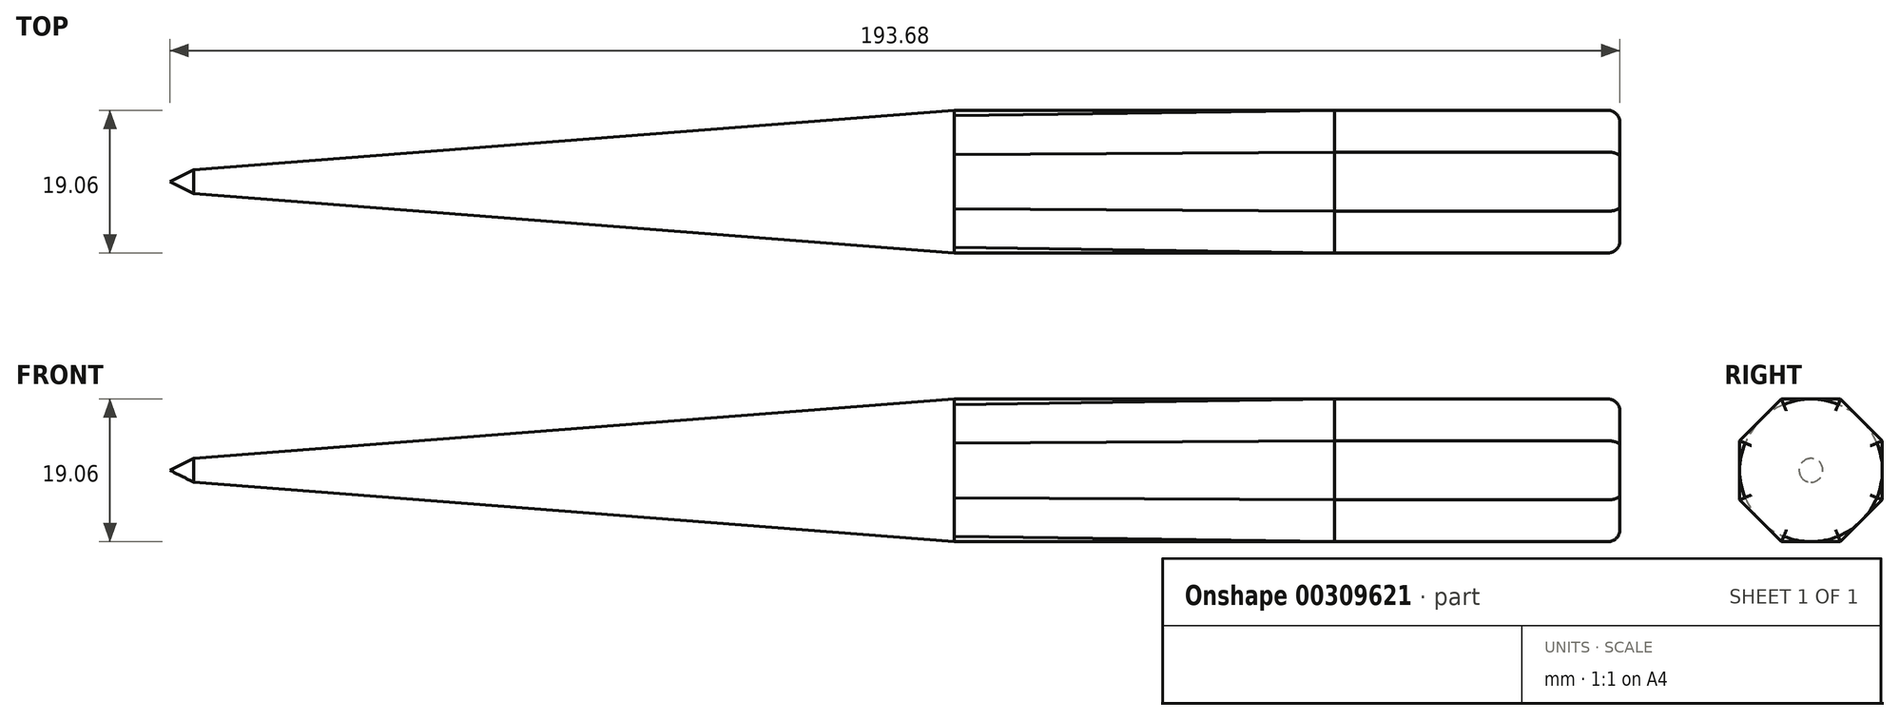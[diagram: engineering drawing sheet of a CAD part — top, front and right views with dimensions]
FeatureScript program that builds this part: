
annotation { "Feature Type Name" : "Feature", "Feature Type Description" : "" }
export const myFeature = defineFeature(function(context is Context, id is Id, definition is map)
    precondition{}
    {
        {
            var Q0;
            Q0=qCreatedBy(makeId("Right.planeOp"),FACE);
            var sketch = newSketch(context, id + "F0", { "sketchPlane" : qUnion([Q0])});
            skCircle(sketch, "E0.cCircle", {"center": v(0, 0) * mm, "radius": 9.53 * mm, "construction": true});
            skLineSegment(sketch, "E0.0", {"start": v(9.53, 3.95) * mm, "end": v(9.53, -3.95) * mm});
            skLineSegment(sketch, "E0.1", {"start": v(9.53, -3.95) * mm, "end": v(3.95, -9.53) * mm});
            skLineSegment(sketch, "E0.2", {"start": v(3.95, -9.53) * mm, "end": v(-3.95, -9.53) * mm});
            skLineSegment(sketch, "E0.3", {"start": v(-3.95, -9.53) * mm, "end": v(-9.53, -3.95) * mm});
            skLineSegment(sketch, "E0.4", {"start": v(-9.53, -3.95) * mm, "end": v(-9.53, 3.95) * mm});
            skLineSegment(sketch, "E0.5", {"start": v(-9.53, 3.95) * mm, "end": v(-3.95, 9.52) * mm});
            skLineSegment(sketch, "E0.6", {"start": v(-3.95, 9.52) * mm, "end": v(3.95, 9.53) * mm});
            skLineSegment(sketch, "E0.7", {"start": v(3.95, 9.53) * mm, "end": v(9.53, 3.95) * mm});
            skPoint(sketch, "E0.0.midPoint", {"position": v(9.53, 0) * mm});
            skSolve(sketch);
        }
        {
            var Q0;
            Q0=makeQuery(id+"F0.imprint","IMPRINT",FACE,{"disambiguationData":[TD([[makeQuery(id+"F0.imprint","IMPRINT",EDGE,{"derivedFrom":sQuery(id+"F0.wireOp",EDGE,"E0.0")}),-1.0]])]});
            extrude(context, id + "F1", {"entities" : qUnion([Q0]), "oppositeDirection" : true, "depth" : 38.1 * mm});
        }
        {
            var Q0;
            Q0=makeQuery(id+"F1.opExtrude","CAP_FACE",FACE,{"disambiguationData":[OSD([sQuery(id+"F0.wireOp",EDGE,"E0.0"),sQuery(id+"F0.wireOp",EDGE,"E0.1"),sQuery(id+"F0.wireOp",EDGE,"E0.2"),sQuery(id+"F0.wireOp",EDGE,"E0.3"),sQuery(id+"F0.wireOp",EDGE,"E0.4"),sQuery(id+"F0.wireOp",EDGE,"E0.5"),sQuery(id+"F0.wireOp",EDGE,"E0.6"),sQuery(id+"F0.wireOp",EDGE,"E0.7")])],"isStart":false});
            cPlane(context, id + "F2", {"entities" : qUnion([Q0]), "cplaneType" : CPlaneType.OFFSET, "offset" : 50.8 * mm, "width" : 152.4 * mm, "height" : 152.4 * mm});
        }
        {
            var Q0;
            Q0=qCreatedBy(id+"F2.planeOp",FACE);
            var sketch = newSketch(context, id + "F3", { "sketchPlane" : qUnion([Q0])});
            skCircle(sketch, "E1", {"center": v(0, 0) * mm, "radius": 9.53 * mm});
            skSolve(sketch);
        }
        {
            var Q1;
            Q1=makeQuery(id+"F1.opExtrude","CAP_FACE",FACE,{"disambiguationData":[OSD([sQuery(id+"F0.wireOp",EDGE,"E0.0"),sQuery(id+"F0.wireOp",EDGE,"E0.1"),sQuery(id+"F0.wireOp",EDGE,"E0.2"),sQuery(id+"F0.wireOp",EDGE,"E0.3"),sQuery(id+"F0.wireOp",EDGE,"E0.4"),sQuery(id+"F0.wireOp",EDGE,"E0.5"),sQuery(id+"F0.wireOp",EDGE,"E0.6"),sQuery(id+"F0.wireOp",EDGE,"E0.7")])],"isStart":false});
            var Q2;
            Q2=makeQuery(id+"F3.imprint","IMPRINT",FACE,{"disambiguationData":[TD([[makeQuery(id+"F3.imprint","IMPRINT",EDGE,{"derivedFrom":sQuery(id+"F3.wireOp",EDGE,"E1")}),1.0]])]});
            loft(context, id + "F4", {"operationType" : NewBodyOperationType.ADD, "sheetProfilesArray" : [{ "sheetProfileEntities" : qUnion([Q1]) }, { "sheetProfileEntities" : qUnion([Q2]) }]});
        }
        {
            var Q0;
            Q0=makeQuery(id+"F4.opLoft","CAP_FACE",FACE,{"disambiguationData":[OSD([makeQuery(id+"F3.imprint","IMPRINT",FACE,{"disambiguationData":[TD([[makeQuery(id+"F3.imprint","IMPRINT",EDGE,{"derivedFrom":sQuery(id+"F3.wireOp",EDGE,"E1")}),1.0]])]})])],"isStart":true});
            cPlane(context, id + "F5", {"entities" : qUnion([Q0]), "cplaneType" : CPlaneType.OFFSET, "offset" : 101.6 * mm, "width" : 152.4 * mm, "height" : 152.4 * mm});
        }
        {
            var Q0;
            Q0=qCreatedBy(id+"F5.planeOp",FACE);
            var sketch = newSketch(context, id + "F6", { "sketchPlane" : qUnion([Q0])});
            skCircle(sketch, "E2", {"center": v(0, 0) * mm, "radius": 1.59 * mm});
            skSolve(sketch);
        }
        {
            var Q1;
            Q1=makeQuery(id+"F4.opLoft","CAP_FACE",FACE,{"disambiguationData":[OSD([makeQuery(id+"F3.imprint","IMPRINT",FACE,{"disambiguationData":[TD([[makeQuery(id+"F3.imprint","IMPRINT",EDGE,{"derivedFrom":sQuery(id+"F3.wireOp",EDGE,"E1")}),1.0]])]})])],"isStart":true});
            var Q2;
            Q2=makeQuery(id+"F6.imprint","IMPRINT",FACE,{"disambiguationData":[TD([[makeQuery(id+"F6.imprint","IMPRINT",EDGE,{"derivedFrom":sQuery(id+"F6.wireOp",EDGE,"E2")}),1.0]])]});
            loft(context, id + "F7", {"operationType" : NewBodyOperationType.ADD, "sheetProfilesArray" : [{ "sheetProfileEntities" : qUnion([Q1]) }, { "sheetProfileEntities" : qUnion([Q2]) }]});
        }
        {
            var Q0;
            Q0=qCreatedBy(id+"F5.planeOp",FACE);
            cPlane(context, id + "F8", {"entities" : qUnion([Q0]), "cplaneType" : CPlaneType.OFFSET, "offset" : 3.17 * mm, "width" : 152.4 * mm, "height" : 152.4 * mm});
        }
        {
            var Q0;
            Q0=qCreatedBy(id+"F8.planeOp",FACE);
            var sketch = newSketch(context, id + "F9", { "sketchPlane" : qUnion([Q0])});
            skPoint(sketch, "E3", {"position": v(0, 0) * mm});
            skSolve(sketch);
        }
        {
            var Q1;
            Q1=sQuery(id+"F9.wireOp",VERTEX,"E3");
            var Q2;
            Q2=makeQuery(id+"F7.opLoft","CAP_FACE",FACE,{"disambiguationData":[OSD([makeQuery(id+"F6.imprint","IMPRINT",FACE,{"disambiguationData":[TD([[makeQuery(id+"F6.imprint","IMPRINT",EDGE,{"derivedFrom":sQuery(id+"F6.wireOp",EDGE,"E2")}),1.0]])]})])],"isStart":true});
            loft(context, id + "F10", {"operationType" : NewBodyOperationType.ADD, "sheetProfilesArray" : [{ "sheetProfileEntities" : qUnion([Q1]) }, { "sheetProfileEntities" : qUnion([Q2]) }]});
        }
        {
            var Q0;
            Q0=makeQuery(id+"F1.opExtrude","CAP_FACE",FACE,{"disambiguationData":[OSD([sQuery(id+"F0.wireOp",EDGE,"E0.0"),sQuery(id+"F0.wireOp",EDGE,"E0.1"),sQuery(id+"F0.wireOp",EDGE,"E0.2"),sQuery(id+"F0.wireOp",EDGE,"E0.3"),sQuery(id+"F0.wireOp",EDGE,"E0.4"),sQuery(id+"F0.wireOp",EDGE,"E0.5"),sQuery(id+"F0.wireOp",EDGE,"E0.6"),sQuery(id+"F0.wireOp",EDGE,"E0.7")])],"isStart":true});
            fillet(context, id + "F11", {"entities" : qUnion([Q0]), "radius" : 1.59 * mm, "tangentPropagation" : true, "allowEdgeOverflow" : false});
        }
    });
